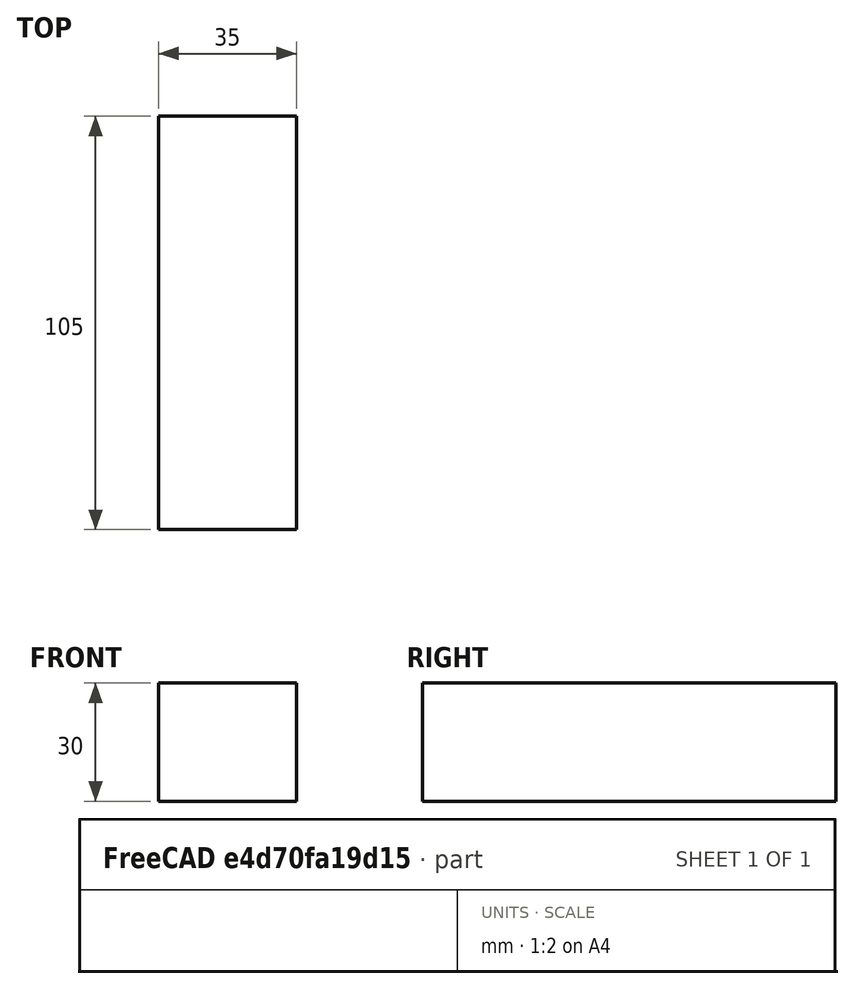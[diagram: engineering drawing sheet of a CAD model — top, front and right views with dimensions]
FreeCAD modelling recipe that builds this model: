
FCSTD DOCUMENT  (FreeCAD 0.18.1R)
Label: baterija3000
License: All rights reserved
LicenseURL: http://en.wikipedia.org/wiki/All_rights_reserved
objects: Sketcher::SketchObject×1, PartDesign::Pad×1, PartDesign::Body×1
note: 4 computed .brp shape members not serialized (recipe doc carries the construction recipe); baked Part::Feature solids carry a one-line shape summary decoded from their .brp

FEATURE [Sketcher::SketchObject] Sketch
  MapMode = 5
  Support = -> [XY_Plane]
  sketch-geometry (4):
    g0: LineSegment StartX=0 StartY=105 StartZ=0 EndX=35 EndY=105 EndZ=0
    g1: LineSegment StartX=35 StartY=105 StartZ=0 EndX=35 EndY=0 EndZ=0
    g2: LineSegment StartX=35 StartY=0 StartZ=0 EndX=0 EndY=0 EndZ=0
    g3: LineSegment StartX=0 StartY=0 StartZ=0 EndX=0 EndY=105 EndZ=0
  constraints (11):
    c: Coincident(g0,g1)
    c: Coincident(g1,g2)
    c: Coincident(g2,g3)
    c: Coincident(g3,g0)
    c: Horizontal(g0)
    c: Horizontal(g2)
    c: Vertical(g1)
    c: Vertical(g3)
    c: Distance(g2) = 35
    c: Distance(g1) = 105
    c: Coincident(g-1,g2)
FEATURE [PartDesign::Pad] Pad
  Length = 30
  Length2 = 100
  Profile = -> Sketch
  Type = 0
FEATURE [PartDesign::Body] Body
  Group = -> [Sketch,Pad]
  Origin = -> Origin
  Tip = -> Pad
